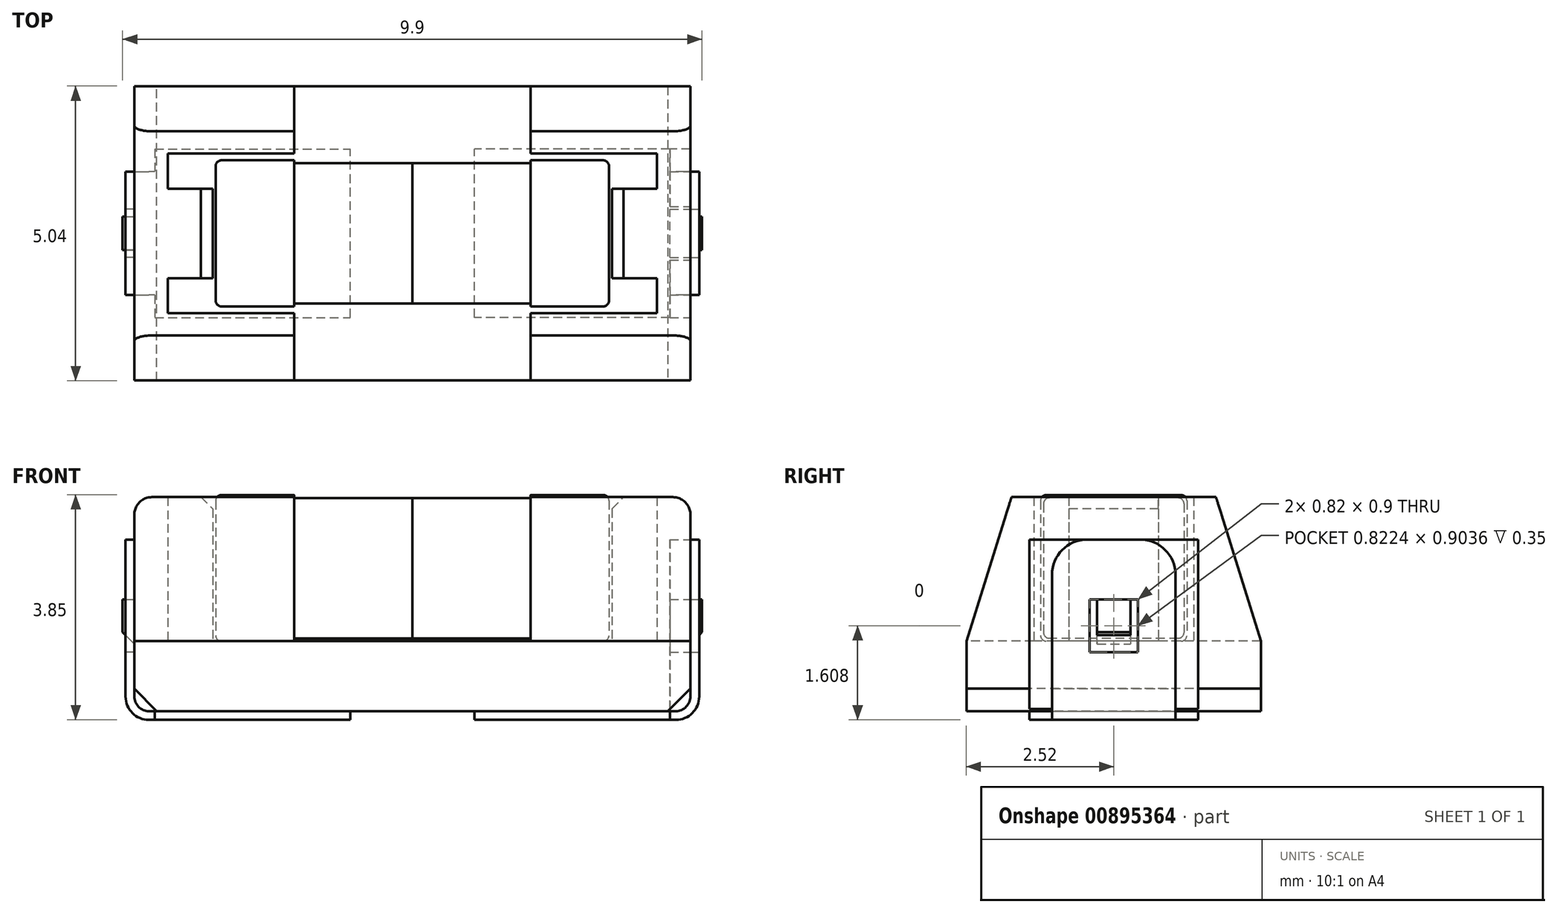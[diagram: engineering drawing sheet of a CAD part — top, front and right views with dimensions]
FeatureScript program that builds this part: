
annotation { "Feature Type Name" : "Feature", "Feature Type Description" : "" }
export const myFeature = defineFeature(function(context is Context, id is Id, definition is map)
    precondition{}
    {
        {
            var Q0;
            Q0=qCreatedBy(makeId("Top.planeOp"),FACE);
            var sketch = newSketch(context, id + "F0", { "sketchPlane" : qUnion([Q0])});
            skLineSegment(sketch, "E0.bottom", {"start": v(-4.75, 2.52) * mm, "end": v(4.75, 2.52) * mm});
            skLineSegment(sketch, "E0.top", {"start": v(-4.75, -2.52) * mm, "end": v(4.75, -2.52) * mm});
            skLineSegment(sketch, "E0.left", {"start": v(-4.75, 2.52) * mm, "end": v(-4.75, -2.52) * mm});
            skLineSegment(sketch, "E0.right", {"start": v(4.75, 2.52) * mm, "end": v(4.75, -2.52) * mm});
            skSolve(sketch);
        }
        {
            var Q0;
            Q0=makeQuery(id+"F0.imprint","IMPRINT",FACE,{"disambiguationData":[TD([[makeQuery(id+"F0.imprint","IMPRINT",EDGE,{"derivedFrom":sQuery(id+"F0.wireOp",EDGE,"E0.bottom")}),-1.0]])]});
            extrude(context, id + "F1", {"entities" : qUnion([Q0]), "depth" : 1.2 * mm, "offsetDistance" : 25 * mm});
        }
        {
            var Q0;
            Q0=makeQuery(id+"F1.opExtrude","CAP_FACE",FACE,{"disambiguationData":[OSD([sQuery(id+"F0.wireOp",EDGE,"E0.bottom"),sQuery(id+"F0.wireOp",EDGE,"E0.top"),sQuery(id+"F0.wireOp",EDGE,"E0.left"),sQuery(id+"F0.wireOp",EDGE,"E0.right")])],"isStart":false});
            var sketch = newSketch(context, id + "F2", { "sketchPlane" : qUnion([Q0])});
            skLineSegment(sketch, "E1", {"start": v(-4.75, 2.52) * mm, "end": v(-2.02, 2.52) * mm});
            skLineSegment(sketch, "E2", {"start": v(-2.02, 2.52) * mm, "end": v(-2.02, 1.37) * mm});
            skLineSegment(sketch, "E3", {"start": v(-2.02, 1.37) * mm, "end": v(-4.18, 1.37) * mm});
            skLineSegment(sketch, "E4", {"start": v(-4.18, 1.36) * mm, "end": v(-4.18, 0.76) * mm});
            skLineSegment(sketch, "E5", {"start": v(-4.18, 0.76) * mm, "end": v(-3.4, 0.77) * mm});
            skLineSegment(sketch, "E6", {"start": v(-3.4, 0.77) * mm, "end": v(-3.4, -0.77) * mm});
            skLineSegment(sketch, "E7", {"start": v(-3.4, -0.77) * mm, "end": v(-4.18, -0.76) * mm});
            skLineSegment(sketch, "E8", {"start": v(-4.18, -0.76) * mm, "end": v(-4.18, -1.37) * mm});
            skLineSegment(sketch, "E9", {"start": v(-4.18, -1.37) * mm, "end": v(-2.02, -1.36) * mm});
            skLineSegment(sketch, "E10", {"start": v(-2.02, -1.36) * mm, "end": v(-2.02, -2.52) * mm});
            skLineSegment(sketch, "E11", {"start": v(-2.02, -2.52) * mm, "end": v(-4.75, -2.52) * mm});
            skLineSegment(sketch, "E12", {"start": v(-4.75, -2.52) * mm, "end": v(-4.75, 2.52) * mm});
            skLineSegment(sketch, "E13.MirrorCS", {"start": v(4.75, 2.52) * mm, "end": v(2.02, 2.52) * mm});
            skLineSegment(sketch, "E14.MirrorCS", {"start": v(4.75, -2.52) * mm, "end": v(4.75, 2.52) * mm});
            skLineSegment(sketch, "E15.MirrorCS", {"start": v(2.02, -2.52) * mm, "end": v(4.75, -2.52) * mm});
            skLineSegment(sketch, "E16.MirrorCS", {"start": v(2.02, -1.36) * mm, "end": v(2.02, -2.52) * mm});
            skLineSegment(sketch, "E17.MirrorCS", {"start": v(4.18, -1.37) * mm, "end": v(2.02, -1.36) * mm});
            skLineSegment(sketch, "E18.MirrorCS", {"start": v(4.18, -0.76) * mm, "end": v(4.18, -1.37) * mm});
            skLineSegment(sketch, "E19.MirrorCS", {"start": v(3.4, -0.77) * mm, "end": v(4.18, -0.76) * mm});
            skLineSegment(sketch, "E20.MirrorCS", {"start": v(3.4, 0.77) * mm, "end": v(3.4, -0.77) * mm});
            skLineSegment(sketch, "E21.MirrorCS", {"start": v(4.18, 0.76) * mm, "end": v(3.4, 0.77) * mm});
            skLineSegment(sketch, "E22.MirrorCS", {"start": v(4.18, 1.36) * mm, "end": v(4.18, 0.76) * mm});
            skLineSegment(sketch, "E23.MirrorCS", {"start": v(2.02, 1.37) * mm, "end": v(4.18, 1.37) * mm});
            skLineSegment(sketch, "E24.MirrorCS", {"start": v(2.02, 2.52) * mm, "end": v(2.02, 1.37) * mm});
            skSolve(sketch);
        }
        {
            var Q0;
            Q0=makeQuery(id+"F2.imprint","IMPRINT",FACE,{"disambiguationData":[TD([[makeQuery(id+"F2.imprint","IMPRINT",EDGE,{"derivedFrom":sQuery(id+"F2.wireOp",EDGE,"E1")}),-1.0]])]});
            var Q1;
            Q1=makeQuery(id+"F2.imprint","IMPRINT",FACE,{"disambiguationData":[TD([[makeQuery(id+"F2.imprint","IMPRINT",EDGE,{"derivedFrom":sQuery(id+"F2.wireOp",EDGE,"E13.MirrorCS")}),-1.0]])]});
            extrude(context, id + "F3", {"entities" : qUnion([Q0, Q1]), "operationType" : NewBodyOperationType.ADD, "depth" : 2.46 * mm, "offsetDistance" : 25 * mm});
        }
        {
            var Q0;
            Q0=makeQuery(id+"F3.boolean.opBoolean","MERGE",FACE,{"derivedFrom":[makeQuery(id+"F1.opExtrude","SWEPT_FACE",FACE,{"disambiguationData":[OSD([sQuery(id+"F0.wireOp",EDGE,"E0.left")])]}),makeQuery(id+"F3.opExtrude","SWEPT_FACE",FACE,{"disambiguationData":[OSD([sQuery(id+"F2.wireOp",EDGE,"E12")])]})]});
            var sketch = newSketch(context, id + "F4", { "sketchPlane" : qUnion([Q0])});
            skLineSegment(sketch, "E25", {"start": v(-2.52, 3.66) * mm, "end": v(-1.75, 3.66) * mm});
            skLineSegment(sketch, "E26", {"start": v(-1.75, 3.66) * mm, "end": v(-2.52, 1.2) * mm});
            skLineSegment(sketch, "E27", {"start": v(-2.52, 1.2) * mm, "end": v(-2.52, 3.66) * mm});
            skPoint(sketch, "E28.0", {"position": v(-2.52, 1.2) * mm});
            skLineSegment(sketch, "E29.MirrorCS", {"start": v(2.52, 3.66) * mm, "end": v(1.75, 3.66) * mm});
            skLineSegment(sketch, "E30.MirrorCS", {"start": v(1.75, 3.66) * mm, "end": v(2.52, 1.2) * mm});
            skLineSegment(sketch, "E31.MirrorCS", {"start": v(2.52, 1.2) * mm, "end": v(2.52, 3.66) * mm});
            skSolve(sketch);
        }
        {
            var Q0;
            Q0=makeQuery(id+"F4.imprint","IMPRINT",FACE,{"disambiguationData":[TD([[makeQuery(id+"F4.imprint","IMPRINT",EDGE,{"derivedFrom":sQuery(id+"F4.wireOp",EDGE,"E25")}),-1.0]])]});
            var Q1;
            Q1=makeQuery(id+"F4.imprint","IMPRINT",FACE,{"disambiguationData":[TD([[makeQuery(id+"F4.imprint","IMPRINT",EDGE,{"derivedFrom":sQuery(id+"F4.wireOp",EDGE,"E29.MirrorCS")}),-1.0]])]});
            extrude(context, id + "F5", {"entities" : qUnion([Q0, Q1]), "operationType" : NewBodyOperationType.REMOVE, "oppositeDirection" : true, "depth" : 25 * mm, "offsetDistance" : 25 * mm});
        }
        {
            var Q0;
            {var subQ0=sQuery(id+"F2.wireOp",EDGE,"E12");var subQ1=sQuery(id+"F4.wireOp",EDGE,"E26");Q0=makeQuery(id+"F5.boolean.opBoolean","COPY",EDGE,{"disambiguationData":[topologyDisambiguationEdgeConnected([makeQuery(id+"F3.opExtrude","CAP_FACE",FACE,{"disambiguationData":[OSD([sQuery(id+"F2.wireOp",EDGE,"E1"),sQuery(id+"F2.wireOp",EDGE,"E2"),sQuery(id+"F2.wireOp",EDGE,"E3"),sQuery(id+"F2.wireOp",EDGE,"E4"),sQuery(id+"F2.wireOp",EDGE,"E5"),sQuery(id+"F2.wireOp",EDGE,"E6"),sQuery(id+"F2.wireOp",EDGE,"E7"),sQuery(id+"F2.wireOp",EDGE,"E8"),sQuery(id+"F2.wireOp",EDGE,"E9"),sQuery(id+"F2.wireOp",EDGE,"E10"),sQuery(id+"F2.wireOp",EDGE,"E11"),subQ0])],"isStart":false})])],"derivedFrom":makeQuery(id+"F5.opExtrude","SWEPT_EDGE",EDGE,{"disambiguationData":[OSD([subQ0,sQuery(id+"F4.wireOp",EDGE,"E25"),subQ1])]})});}
            var Q1;
            Q1=makeQuery(id+"F3.opExtrude","CAP_EDGE",EDGE,{"disambiguationData":[OSD([sQuery(id+"F2.wireOp",EDGE,"E12")])],"isStart":false});
            var Q2;
            {var subQ0=sQuery(id+"F2.wireOp",EDGE,"E12");var subQ1=sQuery(id+"F4.wireOp",EDGE,"E30.MirrorCS");Q2=makeQuery(id+"F5.boolean.opBoolean","COPY",EDGE,{"disambiguationData":[topologyDisambiguationEdgeConnected([makeQuery(id+"F3.opExtrude","CAP_FACE",FACE,{"disambiguationData":[OSD([sQuery(id+"F2.wireOp",EDGE,"E1"),sQuery(id+"F2.wireOp",EDGE,"E2"),sQuery(id+"F2.wireOp",EDGE,"E3"),sQuery(id+"F2.wireOp",EDGE,"E4"),sQuery(id+"F2.wireOp",EDGE,"E5"),sQuery(id+"F2.wireOp",EDGE,"E6"),sQuery(id+"F2.wireOp",EDGE,"E7"),sQuery(id+"F2.wireOp",EDGE,"E8"),sQuery(id+"F2.wireOp",EDGE,"E9"),sQuery(id+"F2.wireOp",EDGE,"E10"),sQuery(id+"F2.wireOp",EDGE,"E11"),subQ0])],"isStart":false})])],"derivedFrom":makeQuery(id+"F5.opExtrude","SWEPT_EDGE",EDGE,{"disambiguationData":[OSD([subQ0,sQuery(id+"F4.wireOp",EDGE,"E29.MirrorCS"),subQ1])]})});}
            var Q3;
            {var subQ0=sQuery(id+"F4.wireOp",EDGE,"E30.MirrorCS");Q3=makeQuery(id+"F5.boolean.opBoolean","COPY",EDGE,{"disambiguationData":[topologyDisambiguationEdgeConnected([makeQuery(id+"F3.opExtrude","CAP_FACE",FACE,{"disambiguationData":[OSD([sQuery(id+"F2.wireOp",EDGE,"E13.MirrorCS"),sQuery(id+"F2.wireOp",EDGE,"E14.MirrorCS"),sQuery(id+"F2.wireOp",EDGE,"E15.MirrorCS"),sQuery(id+"F2.wireOp",EDGE,"E16.MirrorCS"),sQuery(id+"F2.wireOp",EDGE,"E17.MirrorCS"),sQuery(id+"F2.wireOp",EDGE,"E18.MirrorCS"),sQuery(id+"F2.wireOp",EDGE,"E19.MirrorCS"),sQuery(id+"F2.wireOp",EDGE,"E20.MirrorCS"),sQuery(id+"F2.wireOp",EDGE,"E21.MirrorCS"),sQuery(id+"F2.wireOp",EDGE,"E22.MirrorCS"),sQuery(id+"F2.wireOp",EDGE,"E23.MirrorCS"),sQuery(id+"F2.wireOp",EDGE,"E24.MirrorCS")])],"isStart":false})])],"derivedFrom":makeQuery(id+"F5.opExtrude","SWEPT_EDGE",EDGE,{"disambiguationData":[OSD([sQuery(id+"F2.wireOp",EDGE,"E12"),sQuery(id+"F4.wireOp",EDGE,"E29.MirrorCS"),subQ0])]})});}
            var Q4;
            Q4=makeQuery(id+"F3.opExtrude","CAP_EDGE",EDGE,{"disambiguationData":[OSD([sQuery(id+"F2.wireOp",EDGE,"E14.MirrorCS")])],"isStart":false});
            var Q5;
            {var subQ0=sQuery(id+"F4.wireOp",EDGE,"E26");Q5=makeQuery(id+"F5.boolean.opBoolean","COPY",EDGE,{"disambiguationData":[topologyDisambiguationEdgeConnected([makeQuery(id+"F3.opExtrude","CAP_FACE",FACE,{"disambiguationData":[OSD([sQuery(id+"F2.wireOp",EDGE,"E13.MirrorCS"),sQuery(id+"F2.wireOp",EDGE,"E14.MirrorCS"),sQuery(id+"F2.wireOp",EDGE,"E15.MirrorCS"),sQuery(id+"F2.wireOp",EDGE,"E16.MirrorCS"),sQuery(id+"F2.wireOp",EDGE,"E17.MirrorCS"),sQuery(id+"F2.wireOp",EDGE,"E18.MirrorCS"),sQuery(id+"F2.wireOp",EDGE,"E19.MirrorCS"),sQuery(id+"F2.wireOp",EDGE,"E20.MirrorCS"),sQuery(id+"F2.wireOp",EDGE,"E21.MirrorCS"),sQuery(id+"F2.wireOp",EDGE,"E22.MirrorCS"),sQuery(id+"F2.wireOp",EDGE,"E23.MirrorCS"),sQuery(id+"F2.wireOp",EDGE,"E24.MirrorCS")])],"isStart":false})])],"derivedFrom":makeQuery(id+"F5.opExtrude","SWEPT_EDGE",EDGE,{"disambiguationData":[OSD([sQuery(id+"F2.wireOp",EDGE,"E12"),sQuery(id+"F4.wireOp",EDGE,"E25"),subQ0])]})});}
            fillet(context, id + "F6", {"entities" : qUnion([Q0, Q1, Q2, Q3, Q4, Q5]), "radius" : 0.3 * mm, "tangentPropagation" : true, "allowEdgeOverflow" : false});
        }
        {
            var Q0;
            Q0=makeQuery(id+"F1.opExtrude","CAP_EDGE",EDGE,{"disambiguationData":[OSD([sQuery(id+"F0.wireOp",EDGE,"E0.left")])],"isStart":true});
            var Q1;
            Q1=makeQuery(id+"F1.opExtrude","CAP_EDGE",EDGE,{"disambiguationData":[OSD([sQuery(id+"F0.wireOp",EDGE,"E0.right")])],"isStart":true});
            chamfer(context, id + "F7", {"entities" : qUnion([Q0, Q1]), "width" : 0.38 * mm, "tangentPropagation" : true});
        }
        {
            var Q0;
            Q0=makeQuery(id+"F3.opExtrude","CAP_EDGE",EDGE,{"disambiguationData":[OSD([sQuery(id+"F2.wireOp",EDGE,"E20.MirrorCS")])],"isStart":false});
            var Q1;
            Q1=makeQuery(id+"F3.opExtrude","CAP_EDGE",EDGE,{"disambiguationData":[OSD([sQuery(id+"F2.wireOp",EDGE,"E6")])],"isStart":false});
            chamfer(context, id + "F8", {"entities" : qUnion([Q0, Q1]), "width" : 0.2 * mm, "tangentPropagation" : true});
        }
        {
            var Q0;
            Q0=makeQuery(id+"F3.boolean.opBoolean","MERGE",FACE,{"derivedFrom":[makeQuery(id+"F1.opExtrude","SWEPT_FACE",FACE,{"disambiguationData":[OSD([sQuery(id+"F0.wireOp",EDGE,"E0.right")])]}),makeQuery(id+"F3.opExtrude","SWEPT_FACE",FACE,{"disambiguationData":[OSD([sQuery(id+"F2.wireOp",EDGE,"E14.MirrorCS")])]})]});
            var sketch = newSketch(context, id + "F9", { "sketchPlane" : qUnion([Q0])});
            skLineSegment(sketch, "E32.bottom", {"start": v(-0.28, 1.91) * mm, "end": v(0.29, 1.91) * mm});
            skLineSegment(sketch, "E32.top", {"start": v(-0.28, 1.15) * mm, "end": v(0.29, 1.15) * mm});
            skLineSegment(sketch, "E32.left", {"start": v(-0.28, 1.91) * mm, "end": v(-0.28, 1.15) * mm});
            skLineSegment(sketch, "E32.right", {"start": v(0.29, 1.91) * mm, "end": v(0.29, 1.15) * mm});
            skSolve(sketch);
        }
        {
            var Q0;
            Q0=makeQuery(id+"F9.imprint","IMPRINT",FACE,{"disambiguationData":[TD([[makeQuery(id+"F9.imprint","IMPRINT",EDGE,{"derivedFrom":sQuery(id+"F9.wireOp",EDGE,"E32.bottom")}),-1.0]])]});
            extrude(context, id + "F10", {"entities" : qUnion([Q0]), "depth" : 0.2 * mm, "offsetDistance" : 25 * mm});
        }
        {
            var Q0;
            Q0=makeQuery(id+"F10.opExtrude","CAP_EDGE",EDGE,{"disambiguationData":[OSD([sQuery(id+"F9.wireOp",EDGE,"E32.top")])],"isStart":false});
            chamfer(context, id + "F11", {"entities" : qUnion([Q0]), "width" : 0.2 * mm, "tangentPropagation" : true});
        }
        {
            var Q0;
            Q0=makeQuery(id+"F10.opExtrude","SWEPT_BODY",BODY,{"disambiguationData":[OSD([sQuery(id+"F9.wireOp",EDGE,"E32.bottom"),sQuery(id+"F9.wireOp",EDGE,"E32.top"),sQuery(id+"F9.wireOp",EDGE,"E32.left"),sQuery(id+"F9.wireOp",EDGE,"E32.right")])]});
            var Q1;
            Q1=qCreatedBy(makeId("Right.planeOp"),FACE);
            mirror(context, id + "F12", {"entities" : qUnion([Q0]), "mirrorPlane" : qUnion([Q1])});
        }
        {
            var Q0;
            Q0=qCreatedBy(makeId("Front.planeOp"),FACE);
            var sketch = newSketch(context, id + "F13", { "sketchPlane" : qUnion([Q0])});
            skLineSegment(sketch, "E33", {"start": v(1.06, 0) * mm, "end": v(1.06, -0.15) * mm});
            skLineSegment(sketch, "E34", {"start": v(1.06, -0.15) * mm, "end": v(4.5, -0.15) * mm});
            skLineSegment(sketch, "E35", {"start": v(4.9, 0.25) * mm, "end": v(4.9, 2.93) * mm});
            skLineSegment(sketch, "E36", {"start": v(4.9, 2.93) * mm, "end": v(4.75, 2.93) * mm});
            skLineSegment(sketch, "E37", {"start": v(4.75, 2.93) * mm, "end": v(4.75, 0.25) * mm});
            skLineSegment(sketch, "E38", {"start": v(4.5, 0) * mm, "end": v(1.06, 0) * mm});
            skPoint(sketch, "E39.visualSharp", {"position": v(4.75, 0) * mm});
            skArc(sketch, "E39.filletArc", {"start": v(4.5, 0) * mm, "mid": v(4.68, 0.07) * mm, "end": v(4.75, 0.25) * mm});
            skPoint(sketch, "E40.visualSharp", {"position": v(4.9, -0.15) * mm});
            skArc(sketch, "E40.filletArc", {"start": v(4.5, -0.15) * mm, "mid": v(4.78, -0.03) * mm, "end": v(4.9, 0.25) * mm});
            skSolve(sketch);
        }
        {
            var Q0;
            Q0 = qSketchRegion(id + "F13", true);
            extrude(context, id + "F14", {"entities" : qUnion([Q0]), "endBound" : BoundingType.SYMMETRIC, "depth" : 2.88 * mm, "offsetDistance" : 25 * mm});
        }
        {
            var Q0;
            Q0=makeQuery(id+"F14.opExtrude","SWEPT_FACE",FACE,{"disambiguationData":[OSD([sQuery(id+"F13.wireOp",EDGE,"E35")])]});
            var sketch = newSketch(context, id + "F15", { "sketchPlane" : qUnion([Q0])});
            skLineSegment(sketch, "E41.bottom", {"start": v(-0.41, 1.91) * mm, "end": v(0.41, 1.91) * mm});
            skLineSegment(sketch, "E41.top", {"start": v(-0.41, 1) * mm, "end": v(0.41, 1) * mm});
            skLineSegment(sketch, "E41.left", {"start": v(-0.41, 1.91) * mm, "end": v(-0.41, 1) * mm});
            skLineSegment(sketch, "E41.right", {"start": v(0.41, 1.91) * mm, "end": v(0.41, 1) * mm});
            skLineSegment(sketch, "E42.0", {"start": v(-1.44, -0.15) * mm, "end": v(1.44, -0.15) * mm});
            skLineSegment(sketch, "E43.bottom", {"start": v(-1.05, -0.15) * mm, "end": v(1.05, -0.15) * mm});
            skLineSegment(sketch, "E43.top", {"start": v(-0.46, 2.93) * mm, "end": v(0.46, 2.93) * mm});
            skLineSegment(sketch, "E43.left", {"start": v(-1.05, -0.15) * mm, "end": v(-1.06, 2.33) * mm});
            skLineSegment(sketch, "E43.right", {"start": v(1.05, -0.15) * mm, "end": v(1.06, 2.33) * mm});
            skPoint(sketch, "E44.visualSharp", {"position": v(-1.06, 2.93) * mm});
            skArc(sketch, "E44.filletArc", {"start": v(-0.46, 2.93) * mm, "mid": v(-0.88, 2.76) * mm, "end": v(-1.06, 2.33) * mm});
            skPoint(sketch, "E45.visualSharp", {"position": v(1.06, 2.93) * mm});
            skArc(sketch, "E45.filletArc", {"start": v(1.06, 2.33) * mm, "mid": v(0.88, 2.76) * mm, "end": v(0.46, 2.93) * mm});
            skLineSegment(sketch, "E46", {"start": v(-1.44, 0.25) * mm, "end": v(-1.44, -0.15) * mm});
            skLineSegment(sketch, "E47", {"start": v(1.44, 0.25) * mm, "end": v(1.44, -0.15) * mm});
            skSolve(sketch);
        }
        {
            var Q0;
            {var subQ2=sQuery(id+"F15.wireOp",EDGE,"E44.filletArc");Q0=makeQuery(id+"F15.imprint","IMPRINT",FACE,{"disambiguationData":[TD([[makeQuery(id+"F15.imprint","IMPRINT",EDGE,{"derivedFrom":subQ2}),-1.0]])]});}
            var Q1;
            {var subQ0=sQuery(id+"F15.wireOp",EDGE,"E46");Q1=makeQuery(id+"F15.imprint","IMPRINT",FACE,{"disambiguationData":[TD([[makeQuery(id+"F15.imprint","IMPRINT",EDGE,{"derivedFrom":subQ0}),1.0]])]});}
            var Q2;
            {var subQ0=sQuery(id+"F15.wireOp",EDGE,"E47");Q2=makeQuery(id+"F15.imprint","IMPRINT",FACE,{"disambiguationData":[TD([[makeQuery(id+"F15.imprint","IMPRINT",EDGE,{"derivedFrom":subQ0}),-1.0]])]});}
            var Q3;
            {var subQ5=sQuery(id+"F15.wireOp",EDGE,"E45.filletArc");Q3=makeQuery(id+"F15.imprint","IMPRINT",FACE,{"disambiguationData":[TD([[makeQuery(id+"F15.imprint","IMPRINT",EDGE,{"derivedFrom":subQ5}),-1.0]])]});}
            var Q4;
            Q4=makeQuery(id+"F15.imprint","IMPRINT",FACE,{"disambiguationData":[TD([[makeQuery(id+"F15.imprint","IMPRINT",EDGE,{"derivedFrom":sQuery(id+"F15.wireOp",EDGE,"E41.bottom")}),-1.0]])]});
            extrude(context, id + "F16", {"entities" : qUnion([Q0, Q1, Q2, Q3, Q4]), "operationType" : NewBodyOperationType.REMOVE, "oppositeDirection" : true, "depth" : 0.5 * mm, "offsetDistance" : 25 * mm});
        }
        {
            var Q0;
            Q0=makeQuery(id+"F14.opExtrude","SWEPT_BODY",BODY,{"disambiguationData":[OSD([sQuery(id+"F13.wireOp",EDGE,"E33"),sQuery(id+"F13.wireOp",EDGE,"E34"),sQuery(id+"F13.wireOp",EDGE,"E35"),sQuery(id+"F13.wireOp",EDGE,"E36"),sQuery(id+"F13.wireOp",EDGE,"E37"),sQuery(id+"F13.wireOp",EDGE,"E38"),sQuery(id+"F13.wireOp",EDGE,"E39.filletArc"),sQuery(id+"F13.wireOp",EDGE,"E40.filletArc")])]});
            var Q1;
            Q1=qCreatedBy(makeId("Right.planeOp"),FACE);
            mirror(context, id + "F17", {"entities" : qUnion([Q0]), "mirrorPlane" : qUnion([Q1])});
        }
        {
            var Q0;
            Q0=makeQuery(id+"F1.opExtrude","CAP_FACE",FACE,{"disambiguationData":[OSD([sQuery(id+"F0.wireOp",EDGE,"E0.bottom"),sQuery(id+"F0.wireOp",EDGE,"E0.top"),sQuery(id+"F0.wireOp",EDGE,"E0.left"),sQuery(id+"F0.wireOp",EDGE,"E0.right")])],"isStart":false});
            cPlane(context, id + "F18", {"entities" : qUnion([Q0]), "cplaneType" : CPlaneType.OFFSET, "offset" : 0 * mm, "width" : 150 * mm, "height" : 150 * mm});
        }
        {
            var Q0;
            Q0=qCreatedBy(id+"F18.planeOp",FACE);
            var sketch = newSketch(context, id + "F19", { "sketchPlane" : qUnion([Q0])});
            skLineSegment(sketch, "E48.bottom", {"start": v(-3.36, 1.25) * mm, "end": v(-2.02, 1.25) * mm});
            skLineSegment(sketch, "E48.top", {"start": v(-3.36, -1.25) * mm, "end": v(-2.02, -1.25) * mm});
            skLineSegment(sketch, "E48.left", {"start": v(-3.36, 1.25) * mm, "end": v(-3.36, -1.25) * mm});
            skLineSegment(sketch, "E48.right", {"start": v(-2.02, 1.25) * mm, "end": v(-2.02, -1.25) * mm});
            skLineSegment(sketch, "E49.bottom", {"start": v(-2.02, 1.2) * mm, "end": v(0, 1.2) * mm});
            skLineSegment(sketch, "E49.top", {"start": v(-2.02, -1.2) * mm, "end": v(0, -1.2) * mm});
            skLineSegment(sketch, "E49.left", {"start": v(-2.02, 1.2) * mm, "end": v(-2.02, -1.2) * mm});
            skLineSegment(sketch, "E49.right", {"start": v(0, 1.2) * mm, "end": v(0, -1.2) * mm});
            skSolve(sketch);
        }
        {
            var Q0;
            {var subQ1=sQuery(id+"F19.wireOp",EDGE,"E48.bottom");Q0=makeQuery(id+"F19.imprint","IMPRINT",FACE,{"disambiguationData":[TD([[makeQuery(id+"F19.imprint","IMPRINT",EDGE,{"derivedFrom":subQ1}),-1.0]])]});}
            extrude(context, id + "F20", {"entities" : qUnion([Q0]), "depth" : 2.5 * mm, "offsetDistance" : 25 * mm});
        }
        {
            var Q0;
            Q0=makeQuery(id+"F19.imprint","IMPRINT",FACE,{"disambiguationData":[TD([[makeQuery(id+"F19.imprint","IMPRINT",EDGE,{"derivedFrom":sQuery(id+"F19.wireOp",EDGE,"E49.bottom")}),-1.0]])]});
            extrude(context, id + "F21", {"entities" : qUnion([Q0]), "depth" : 2.45 * mm, "offsetDistance" : 25 * mm, "hasSecondDirection" : true, "secondDirectionOppositeDirection" : false, "secondDirectionDepth" : 0.05 * mm});
        }
        {
            var Q0;
            Q0=makeQuery(id+"F20.opExtrude","CAP_EDGE",EDGE,{"disambiguationData":[OSD([sQuery(id+"F19.wireOp",EDGE,"E48.top")])],"isStart":false});
            var Q1;
            Q1=makeQuery(id+"F20.opExtrude","CAP_EDGE",EDGE,{"disambiguationData":[OSD([sQuery(id+"F19.wireOp",EDGE,"E48.bottom")])],"isStart":false});
            var Q2;
            Q2=makeQuery(id+"F20.opExtrude","SWEPT_EDGE",EDGE,{"disambiguationData":[OSD([sQuery(id+"F19.wireOp",EDGE,"E48.bottom"),sQuery(id+"F19.wireOp",EDGE,"E48.left")])]});
            var Q3;
            Q3=makeQuery(id+"F20.opExtrude","SWEPT_FACE",FACE,{"disambiguationData":[OSD([sQuery(id+"F19.wireOp",EDGE,"E48.left")])]});
            var Q4;
            Q4=makeQuery(id+"F20.opExtrude","CAP_EDGE",EDGE,{"disambiguationData":[OSD([sQuery(id+"F19.wireOp",EDGE,"E48.top")])],"isStart":true});
            var Q5;
            Q5=makeQuery(id+"F20.opExtrude","CAP_EDGE",EDGE,{"disambiguationData":[OSD([sQuery(id+"F19.wireOp",EDGE,"E48.bottom")])],"isStart":true});
            fillet(context, id + "F22", {"entities" : qUnion([Q0, Q1, Q2, Q3, Q4, Q5]), "radius" : 0.1 * mm, "tangentPropagation" : true, "allowEdgeOverflow" : false});
        }
        {
            var Q0;
            Q0=makeQuery(id+"F21.opExtrude","CAP_EDGE",EDGE,{"disambiguationData":[OSD([sQuery(id+"F19.wireOp",EDGE,"E49.top")])],"isStart":false});
            var Q1;
            Q1=makeQuery(id+"F21.opExtrude","CAP_EDGE",EDGE,{"disambiguationData":[OSD([sQuery(id+"F19.wireOp",EDGE,"E49.bottom")])],"isStart":false});
            var Q2;
            Q2=makeQuery(id+"F21.opExtrude","CAP_EDGE",EDGE,{"disambiguationData":[OSD([sQuery(id+"F19.wireOp",EDGE,"E49.bottom")])],"isStart":true});
            var Q3;
            Q3=makeQuery(id+"F21.opExtrude","CAP_EDGE",EDGE,{"disambiguationData":[OSD([sQuery(id+"F19.wireOp",EDGE,"E49.top")])],"isStart":true});
            fillet(context, id + "F23", {"entities" : qUnion([Q0, Q1, Q2, Q3]), "radius" : 0.1 * mm, "tangentPropagation" : true, "allowEdgeOverflow" : false});
        }
        {
            var Q0;
            Q0=makeQuery(id+"F21.opExtrude","SWEPT_BODY",BODY,{"disambiguationData":[OSD([sQuery(id+"F19.wireOp",EDGE,"E49.bottom"),sQuery(id+"F19.wireOp",EDGE,"E49.top"),sQuery(id+"F19.wireOp",EDGE,"E49.left"),sQuery(id+"F19.wireOp",EDGE,"E49.right")])]});
            var Q1;
            Q1=makeQuery(id+"F20.opExtrude","SWEPT_BODY",BODY,{"disambiguationData":[OSD([sQuery(id+"F19.wireOp",EDGE,"E48.bottom"),sQuery(id+"F19.wireOp",EDGE,"E48.top"),sQuery(id+"F19.wireOp",EDGE,"E48.left"),sQuery(id+"F19.wireOp",EDGE,"E48.right"),sQuery(id+"F19.wireOp",EDGE,"E49.left")])]});
            var Q2;
            Q2=qCreatedBy(makeId("Right.planeOp"),FACE);
            mirror(context, id + "F24", {"entities" : qUnion([Q0, Q1]), "mirrorPlane" : qUnion([Q2])});
        }
    });
